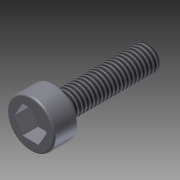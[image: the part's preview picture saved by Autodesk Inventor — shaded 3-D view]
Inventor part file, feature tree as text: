
AUTODESK INVENTOR PART (.ipt)
format: ipt  version: 2012 (Build 160160000, 160)  size: 114,176 bytes
history: native  units: in
note: dims shown in document units (in); Inventor stores cm internally (conversion verified against a paired STEP export)
features: extrude x3, sketch x1, thread x1, chamfer x1, fillet x1
ambient origin geometry x8: Origin, YZ Plane, XZ Plane, XY Plane, X Axis, Y Axis, Z Axis, Center Point
bodies: Solid1 (feature_tree)
feature tree (7):
  sketch  "Sketch1"  dims[d0=0.19in d1=0.375in d2=0.2188in d3=0.75in d4=0.0in d5=0.1875in d6=0.0in d7=0.065in d8=0.0in d9=1.0in d10=0.0in d11=0.0156in d12=0.125in d13=45.0deg d14=0.0156in]
  extrude  "Extrusion1"  Depth=0.375in
  extrude  "Extrusion2"  Depth=0.2188in
  extrude  "Extrusion3"  Depth=0.75in TaperAngle=0.0deg
  thread  "Thread1"  [1 undecoded]
  chamfer  "Chamfer1"  Distance=0.065in
  fillet  "Fillet1"  Radius=1.0in
note: 1 required parameter value undecoded (feature->parameter linkage not recoverable at this tier; creation-order binding heuristic only, values carry confidence <= 0.55)
